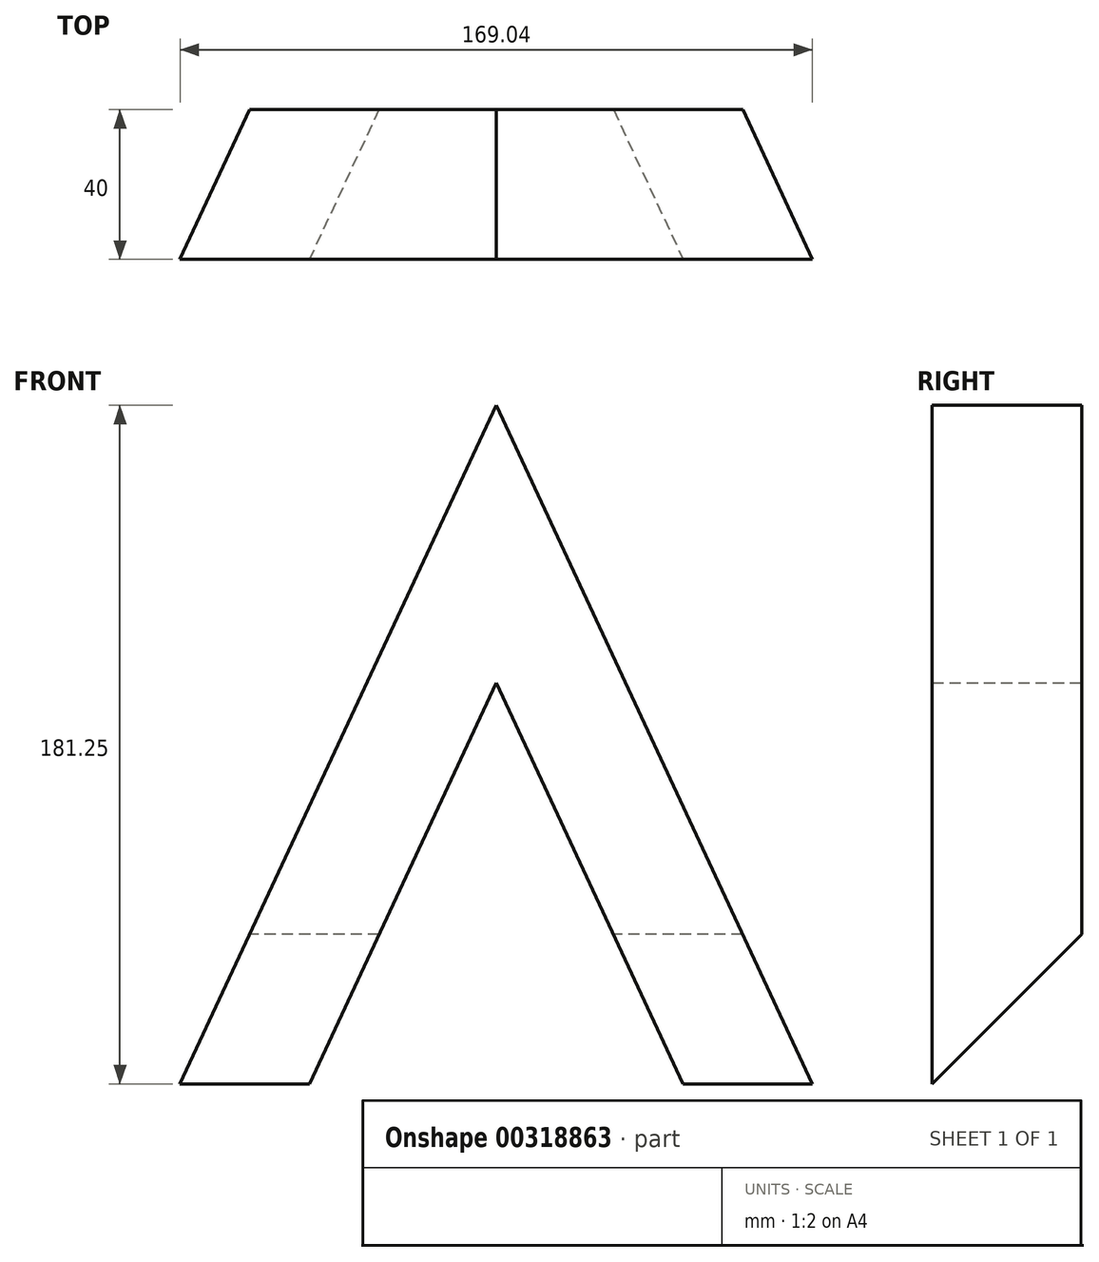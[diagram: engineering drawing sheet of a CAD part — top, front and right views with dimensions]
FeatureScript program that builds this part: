
annotation { "Feature Type Name" : "Feature", "Feature Type Description" : "" }
export const myFeature = defineFeature(function(context is Context, id is Id, definition is map)
    precondition{}
    {
        {
            var Q0;
            Q0=qCreatedBy(makeId("Front.planeOp"),FACE);
            var sketch = newSketch(context, id + "F0", { "sketchPlane" : qUnion([Q0])});
            skLineSegment(sketch, "E0.top", {"start": v(-84.52, -107.16) * mm, "end": v(-49.97, -107.16) * mm});
            skLineSegment(sketch, "E1", {"start": v(-84.52, -107.16) * mm, "end": v(0, 74.1) * mm});
            skLineSegment(sketch, "E2", {"start": v(0, 0) * mm, "end": v(-49.97, -107.16) * mm});
            skLineSegment(sketch, "E3.MirrorCS", {"start": v(84.52, -107.16) * mm, "end": v(0, 74.1) * mm});
            skLineSegment(sketch, "E4.MirrorCS", {"start": v(84.52, -107.16) * mm, "end": v(49.97, -107.16) * mm});
            skLineSegment(sketch, "E5.MirrorCS", {"start": v(0, 0) * mm, "end": v(49.97, -107.16) * mm});
            skSolve(sketch);
        }
        {
            var Q0;
            Q0=makeQuery(id+"F0.imprint","IMPRINT",FACE,{"disambiguationData":[TD([[makeQuery(id+"F0.imprint","IMPRINT",EDGE,{"derivedFrom":sQuery(id+"F0.wireOp",EDGE,"E0.top")}),1.0]])]});
            extrude(context, id + "F1", {"entities" : qUnion([Q0]), "depth" : 40 * mm});
        }
        {
            var Q0;
            Q0=qCreatedBy(makeId("Right.planeOp"),FACE);
            var sketch = newSketch(context, id + "F2", { "sketchPlane" : qUnion([Q0])});
            skLineSegment(sketch, "E6", {"start": v(-40, -107.15) * mm, "end": v(0, -67.15) * mm});
            skLineSegment(sketch, "E7", {"start": v(-40, -107.15) * mm, "end": v(0, -107.15) * mm});
            skLineSegment(sketch, "E8", {"start": v(0, -107.15) * mm, "end": v(0, -72.66) * mm});
            skLineSegment(sketch, "E9.trimOffspring", {"start": v(0, -72.66) * mm, "end": v(0, -107.15) * mm, "construction": true});
            skPoint(sketch, "E10.orphan", {"position": v(0, 94.16) * mm});
            skLineSegment(sketch, "E11", {"start": v(0, -72.66) * mm, "end": v(0, -67.15) * mm});
            skSolve(sketch);
        }
        {
            var Q0;
            Q0=makeQuery(id+"F2.imprint","IMPRINT",FACE,{"disambiguationData":[TD([[makeQuery(id+"F2.imprint","IMPRINT",EDGE,{"derivedFrom":sQuery(id+"F2.wireOp",EDGE,"E6")}),-1.0]])]});
            extrude(context, id + "F3", {"entities" : qUnion([Q0]), "operationType" : NewBodyOperationType.REMOVE, "endBound" : BoundingType.SYMMETRIC, "depth" : 288 * mm});
        }
    });
